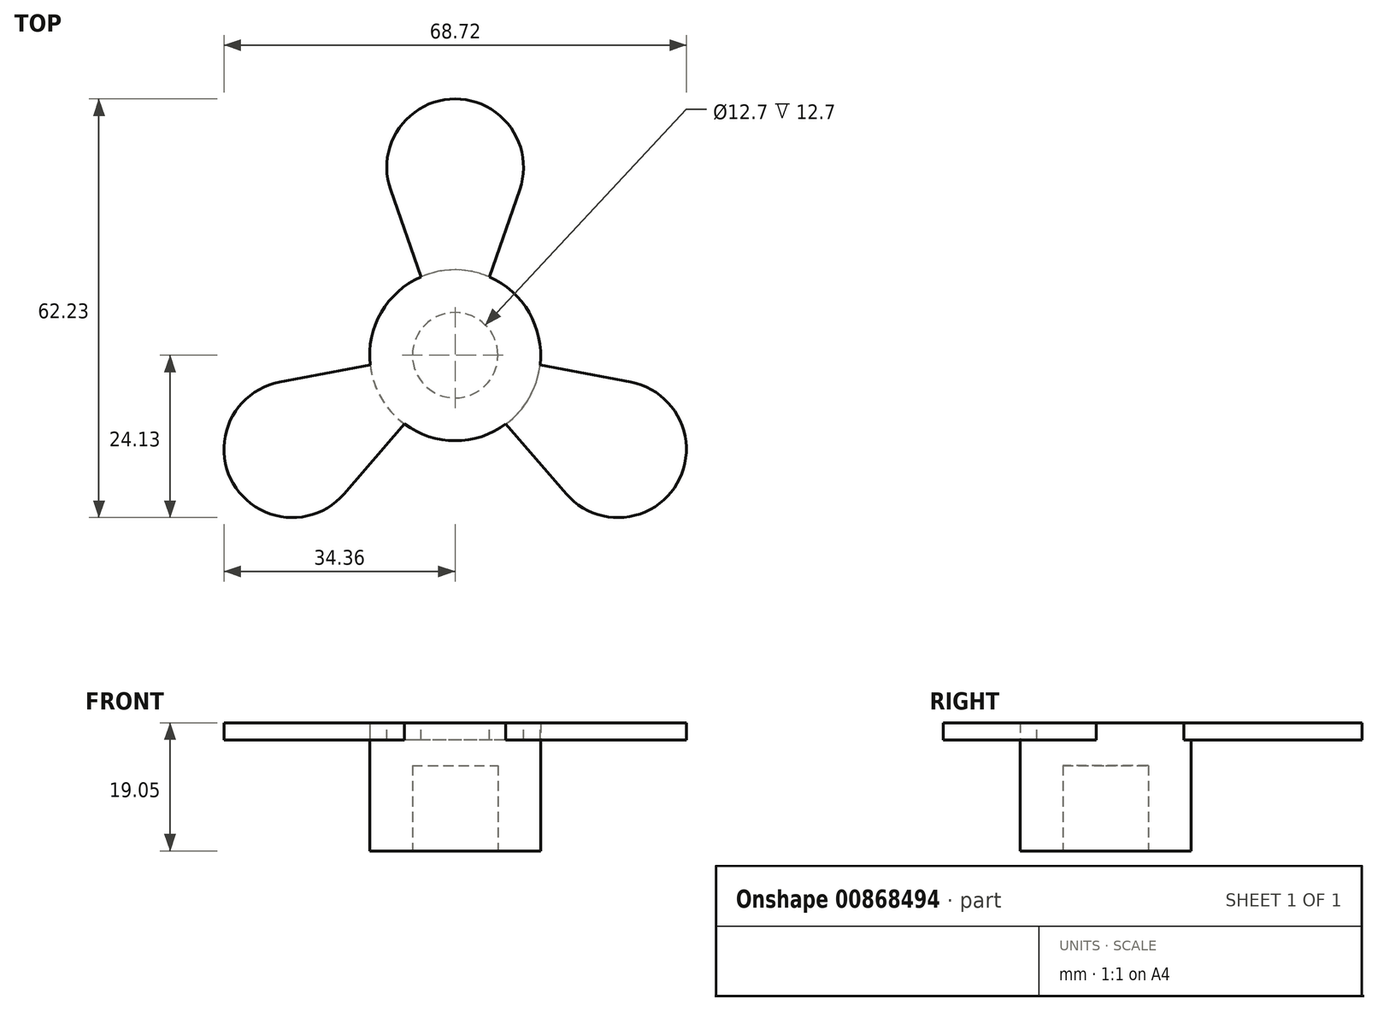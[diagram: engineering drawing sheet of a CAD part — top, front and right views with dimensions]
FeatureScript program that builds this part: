
annotation { "Feature Type Name" : "Feature", "Feature Type Description" : "" }
export const myFeature = defineFeature(function(context is Context, id is Id, definition is map)
    precondition{}
    {
        {
            var Q0;
            Q0=qCreatedBy(makeId("Top.planeOp"),FACE);
            var sketch = newSketch(context, id + "F0", { "sketchPlane" : qUnion([Q0])});
            skCircle(sketch, "E0", {"center": v(0, 0) * mm, "radius": 12.7 * mm});
            skSolve(sketch);
        }
        {
            var Q0;
            Q0 = qSketchRegion(id + "F0", true);
            extrude(context, id + "F1", {"entities" : qUnion([Q0]), "depth" : 19.05 * mm, "offsetDistance" : 25.4 * mm});
        }
        {
            var Q0;
            Q0=makeQuery(id+"F1.opExtrude","CAP_FACE",FACE,{"disambiguationData":[OSD([sQuery(id+"F0.wireOp",EDGE,"E0")])],"isStart":true});
            var sketch = newSketch(context, id + "F2", { "sketchPlane" : qUnion([Q0])});
            skCircle(sketch, "E1", {"center": v(0, 0) * mm, "radius": 6.35 * mm});
            skSolve(sketch);
        }
        {
            var Q0;
            Q0 = qSketchRegion(id + "F2", true);
            extrude(context, id + "F3", {"entities" : qUnion([Q0]), "operationType" : NewBodyOperationType.REMOVE, "oppositeDirection" : true, "depth" : 12.7 * mm, "offsetDistance" : 25.4 * mm});
        }
        {
            var Q0;
            Q0=makeQuery(id+"F1.opExtrude","CAP_FACE",FACE,{"disambiguationData":[OSD([sQuery(id+"F0.wireOp",EDGE,"E0")])],"isStart":false});
            var sketch = newSketch(context, id + "F4", { "sketchPlane" : qUnion([Q0])});
            skLineSegment(sketch, "E2", {"start": v(0, 0) * mm, "end": v(0, 38.1) * mm, "construction": true});
            skLineSegment(sketch, "E3", {"start": v(0, 0) * mm, "end": v(33, -19.05) * mm, "construction": true});
            skLineSegment(sketch, "E4", {"start": v(0, 0) * mm, "end": v(-33, -19.05) * mm, "construction": true});
            skCircle(sketch, "E5", {"center": v(0, 27.94) * mm, "radius": 10.16 * mm});
            skLineSegment(sketch, "E6", {"start": v(-5.08, 11.64) * mm, "end": v(-9.6, 24.6) * mm});
            skLineSegment(sketch, "E7", {"start": v(9.6, 24.6) * mm, "end": v(5.08, 11.64) * mm});
            skCircle(sketch, "E8.1.0", {"center": v(-24.2, -13.97) * mm, "radius": 10.16 * mm});
            skLineSegment(sketch, "E8.1.1", {"start": v(-7.54, -10.22) * mm, "end": v(-16.5, -20.6) * mm});
            skLineSegment(sketch, "E8.1.2", {"start": v(-26.1, -3.99) * mm, "end": v(-12.62, -1.42) * mm});
            skCircle(sketch, "E8.2.0", {"center": v(24.2, -13.97) * mm, "radius": 10.16 * mm});
            skLineSegment(sketch, "E8.2.1", {"start": v(12.62, -1.42) * mm, "end": v(26.1, -3.99) * mm});
            skLineSegment(sketch, "E8.2.2", {"start": v(16.5, -20.6) * mm, "end": v(7.54, -10.22) * mm});
            skPoint(sketch, "E8.center", {"position": v(0, 0) * mm});
            skCircle(sketch, "E9", {"center": v(0, 0) * mm, "radius": 12.7 * mm});
            skSolve(sketch);
        }
        {
            var Q0;
            Q0 = qSketchRegion(id + "F4", true);
            extrude(context, id + "F5", {"entities" : qUnion([Q0]), "operationType" : NewBodyOperationType.ADD, "oppositeDirection" : true, "depth" : 2.54 * mm, "offsetDistance" : 25.4 * mm});
        }
    });
